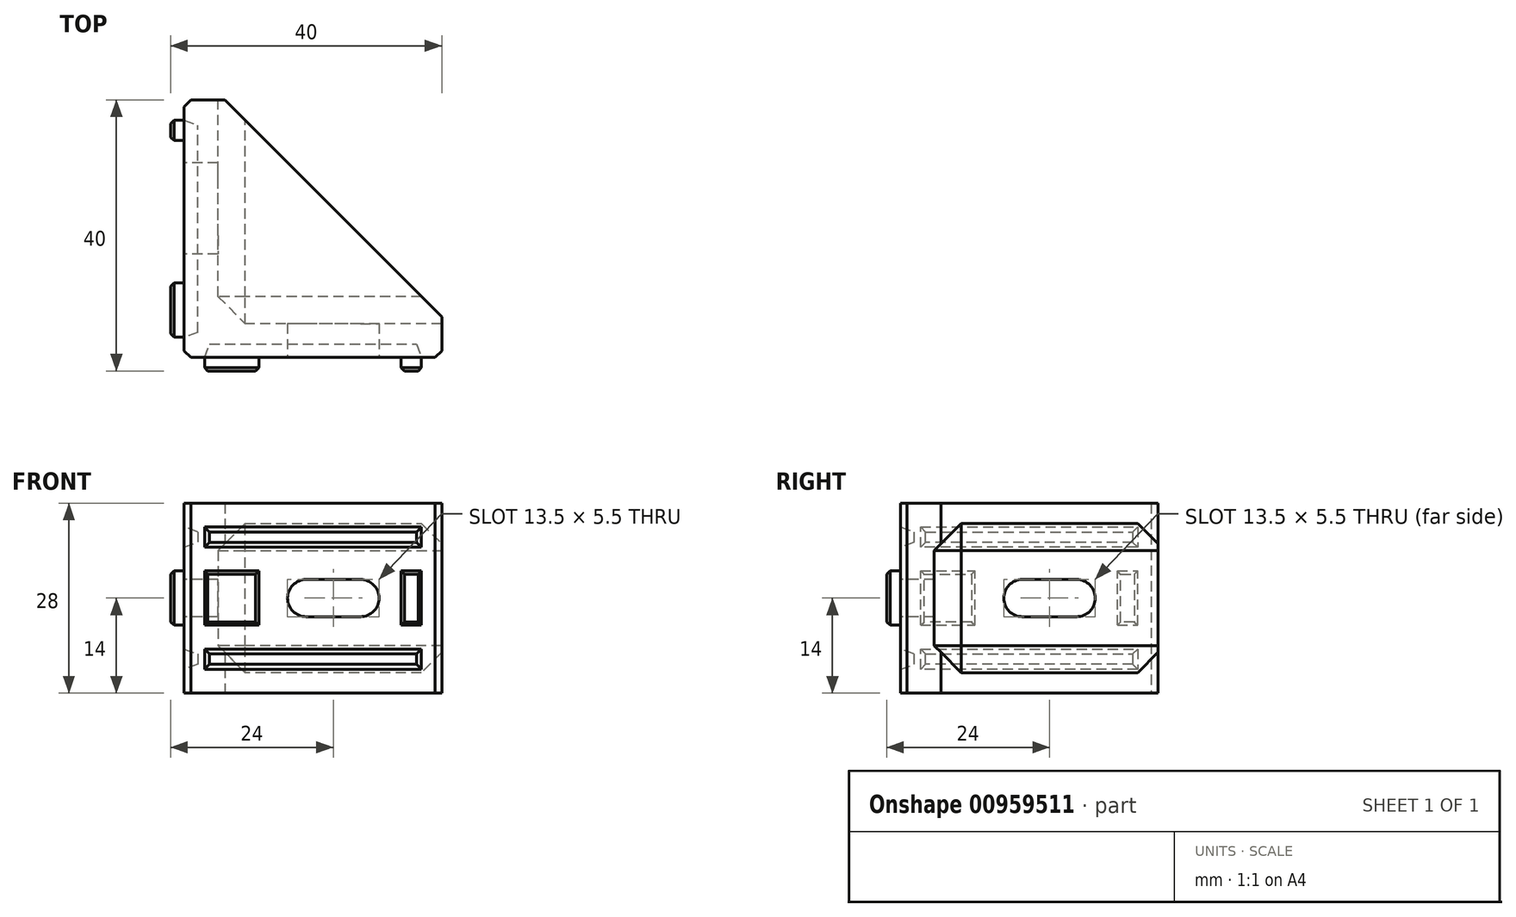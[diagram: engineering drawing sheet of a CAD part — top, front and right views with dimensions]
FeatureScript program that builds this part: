
annotation { "Feature Type Name" : "Feature", "Feature Type Description" : "" }
export const myFeature = defineFeature(function(context is Context, id is Id, definition is map)
    precondition{}
    {
        {
            var Q0;
            Q0=qCreatedBy(makeId("Top.planeOp"),FACE);
            var sketch = newSketch(context, id + "F0", { "sketchPlane" : qUnion([Q0])});
            skLineSegment(sketch, "E0.bottom", {"start": v(19, -19) * mm, "end": v(-19, -19) * mm});
            skLineSegment(sketch, "E0.top", {"start": v(-13, 19) * mm, "end": v(-19, 19) * mm});
            skLineSegment(sketch, "E0.left", {"start": v(19, -19) * mm, "end": v(19, -13) * mm});
            skLineSegment(sketch, "E0.right", {"start": v(-19, -19) * mm, "end": v(-19, 19) * mm});
            skPoint(sketch, "E0.middle", {"position": v(0, 0) * mm});
            skLineSegment(sketch, "E1", {"start": v(-13, 19) * mm, "end": v(19, -13) * mm});
            skSolve(sketch);
        }
        {
            var Q0;
            Q0 = qSketchRegion(id + "F0", true);
            extrude(context, id + "F1", {"entities" : qUnion([Q0]), "depth" : 28 * mm, "offsetDistance" : 25 * mm});
        }
        {
            var Q0;
            Q0=makeQuery(id+"F1.opExtrude","SWEPT_FACE",FACE,{"disambiguationData":[OSD([sQuery(id+"F0.wireOp",EDGE,"E0.left")])]});
            var sketch = newSketch(context, id + "F2", { "sketchPlane" : qUnion([Q0])});
            skLineSegment(sketch, "E2.0", {"start": v(19, 28) * mm, "end": v(19, 0) * mm});
            skLineSegment(sketch, "E3", {"start": v(19, 25) * mm, "end": v(-14, 25) * mm});
            skLineSegment(sketch, "E4", {"start": v(-14, 25) * mm, "end": v(-14, 3) * mm});
            skLineSegment(sketch, "E5", {"start": v(-14, 3) * mm, "end": v(19, 3) * mm});
            skSolve(sketch);
        }
        {
            var Q0;
            Q0 = qSketchRegion(id + "F2", true);
            var Q1;
            Q1=makeQuery(id+"F1.opExtrude","SWEPT_FACE",FACE,{"disambiguationData":[OSD([sQuery(id+"F0.wireOp",EDGE,"E0.right")])]});
            extrude(context, id + "F3", {"entities" : qUnion([Q0]), "operationType" : NewBodyOperationType.REMOVE, "endBound" : BoundingType.UP_TO_SURFACE, "oppositeDirection" : true, "depth" : 25 * mm, "endBoundEntityFace" : qUnion([Q1]), "hasOffset" : true, "offsetDistance" : 5 * mm});
        }
        {
            var Q0;
            Q0=makeQuery(id+"F1.opExtrude","SWEPT_FACE",FACE,{"disambiguationData":[OSD([sQuery(id+"F0.wireOp",EDGE,"E0.bottom")])]});
            var sketch = newSketch(context, id + "F4", { "sketchPlane" : qUnion([Q0])});
            skLineSegment(sketch, "E6.0", {"start": v(-14, 25) * mm, "end": v(-14, 3) * mm, "construction": true});
            skLineSegment(sketch, "E7", {"start": v(19, 14) * mm, "end": v(-14, 14) * mm, "construction": true});
            skArc(sketch, "E8", {"start": v(7, 11.25) * mm, "mid": v(9.75, 14) * mm, "end": v(7, 16.75) * mm});
            skArc(sketch, "E9", {"start": v(-1, 16.75) * mm, "mid": v(-3.75, 14) * mm, "end": v(-1, 11.25) * mm});
            skLineSegment(sketch, "E10", {"start": v(7, 16.75) * mm, "end": v(-1, 16.75) * mm});
            skLineSegment(sketch, "E11", {"start": v(7, 11.25) * mm, "end": v(-1, 11.25) * mm});
            skLineSegment(sketch, "E12.bottom", {"start": v(-8, 10) * mm, "end": v(-16, 10) * mm});
            skLineSegment(sketch, "E12.top", {"start": v(-8, 18) * mm, "end": v(-16, 18) * mm});
            skLineSegment(sketch, "E12.left", {"start": v(-8, 10) * mm, "end": v(-8, 18) * mm});
            skLineSegment(sketch, "E12.right", {"start": v(-16, 10) * mm, "end": v(-16, 18) * mm});
            skPoint(sketch, "E12.middle", {"position": v(-12, 14) * mm});
            skLineSegment(sketch, "E13.bottom", {"start": v(16, 10) * mm, "end": v(13, 10) * mm});
            skLineSegment(sketch, "E13.top", {"start": v(16, 18) * mm, "end": v(13, 18) * mm});
            skLineSegment(sketch, "E13.left", {"start": v(16, 10) * mm, "end": v(16, 18) * mm});
            skLineSegment(sketch, "E13.right", {"start": v(13, 10) * mm, "end": v(13, 18) * mm});
            skPoint(sketch, "E13.middle", {"position": v(14.5, 14) * mm});
            skLineSegment(sketch, "E14.bottom", {"start": v(-16, 24.5) * mm, "end": v(16, 24.5) * mm});
            skLineSegment(sketch, "E14.top", {"start": v(-16, 21.5) * mm, "end": v(16, 21.5) * mm});
            skLineSegment(sketch, "E14.left", {"start": v(-16, 24.5) * mm, "end": v(-16, 21.5) * mm});
            skLineSegment(sketch, "E14.right", {"start": v(16, 24.5) * mm, "end": v(16, 21.5) * mm});
            skLineSegment(sketch, "E15.MirrorCS", {"start": v(-16, 6.5) * mm, "end": v(16, 6.5) * mm});
            skLineSegment(sketch, "E16.MirrorCS", {"start": v(-16, 3.5) * mm, "end": v(16, 3.5) * mm});
            skLineSegment(sketch, "E17.MirrorCS", {"start": v(-16, 3.5) * mm, "end": v(-16, 6.5) * mm});
            skLineSegment(sketch, "E18.MirrorCS", {"start": v(16, 3.5) * mm, "end": v(16, 6.5) * mm});
            skSolve(sketch);
        }
        {
            var Q0;
            Q0=makeQuery(id+"F1.opExtrude","SWEPT_FACE",FACE,{"disambiguationData":[OSD([sQuery(id+"F0.wireOp",EDGE,"E0.right")])]});
            var sketch = newSketch(context, id + "F5", { "sketchPlane" : qUnion([Q0])});
            skLineSegment(sketch, "E19", {"start": v(14, 14) * mm, "end": v(-19, 14) * mm, "construction": true});
            skArc(sketch, "E20", {"start": v(1, 11.25) * mm, "mid": v(3.75, 14) * mm, "end": v(1, 16.75) * mm});
            skArc(sketch, "E21", {"start": v(-7, 16.75) * mm, "mid": v(-9.75, 14) * mm, "end": v(-7, 11.25) * mm});
            skLineSegment(sketch, "E22", {"start": v(1, 16.75) * mm, "end": v(-7, 16.75) * mm});
            skLineSegment(sketch, "E23", {"start": v(1, 11.25) * mm, "end": v(-7, 11.25) * mm});
            skLineSegment(sketch, "E24.0", {"start": v(14, 25) * mm, "end": v(14, 3) * mm, "construction": true});
            skLineSegment(sketch, "E25.bottom", {"start": v(16, 10) * mm, "end": v(8, 10) * mm});
            skLineSegment(sketch, "E25.top", {"start": v(16, 18) * mm, "end": v(8, 18) * mm});
            skLineSegment(sketch, "E25.left", {"start": v(16, 10) * mm, "end": v(16, 18) * mm});
            skLineSegment(sketch, "E25.right", {"start": v(8, 10) * mm, "end": v(8, 18) * mm});
            skPoint(sketch, "E25.middle", {"position": v(12, 14) * mm});
            skLineSegment(sketch, "E26.bottom", {"start": v(-13, 10) * mm, "end": v(-16, 10) * mm});
            skLineSegment(sketch, "E26.top", {"start": v(-13, 18) * mm, "end": v(-16, 18) * mm});
            skLineSegment(sketch, "E26.left", {"start": v(-13, 10) * mm, "end": v(-13, 18) * mm});
            skLineSegment(sketch, "E26.right", {"start": v(-16, 10) * mm, "end": v(-16, 18) * mm});
            skPoint(sketch, "E26.middle", {"position": v(-14.5, 14) * mm});
            skLineSegment(sketch, "E27.bottom", {"start": v(-16, 21.5) * mm, "end": v(16, 21.5) * mm});
            skLineSegment(sketch, "E27.top", {"start": v(-16, 24.5) * mm, "end": v(16, 24.5) * mm});
            skLineSegment(sketch, "E27.left", {"start": v(-16, 21.5) * mm, "end": v(-16, 24.5) * mm});
            skLineSegment(sketch, "E27.right", {"start": v(16, 21.5) * mm, "end": v(16, 24.5) * mm});
            skLineSegment(sketch, "E28.MirrorCS", {"start": v(-16, 6.5) * mm, "end": v(16, 6.5) * mm});
            skLineSegment(sketch, "E29.MirrorCS", {"start": v(16, 6.5) * mm, "end": v(16, 3.5) * mm});
            skLineSegment(sketch, "E30.MirrorCS", {"start": v(-16, 3.5) * mm, "end": v(16, 3.5) * mm});
            skLineSegment(sketch, "E31.MirrorCS", {"start": v(-16, 6.5) * mm, "end": v(-16, 3.5) * mm});
            skSolve(sketch);
        }
        {
            var Q0;
            Q0=makeQuery(id+"F4.imprint","IMPRINT",FACE,{"disambiguationData":[TD([[makeQuery(id+"F4.imprint","IMPRINT",EDGE,{"derivedFrom":sQuery(id+"F4.wireOp",EDGE,"E8")}),1.0]])]});
            var Q1;
            Q1 = qConstructionFilter(qBodyType(qCreatedBy(id + "F4" ,EDGE), BodyType.WIRE), ConstructionObject.NO);
            extrude(context, id + "F6", {"entities" : qUnion([Q0]), "operationType" : NewBodyOperationType.REMOVE, "surfaceEntities" : qUnion([Q1]), "oppositeDirection" : true, "depth" : 25 * mm, "offsetDistance" : 25 * mm});
        }
        {
            var Q0;
            Q0=makeQuery(id+"F5.imprint","IMPRINT",FACE,{"disambiguationData":[TD([[makeQuery(id+"F5.imprint","IMPRINT",EDGE,{"derivedFrom":sQuery(id+"F5.wireOp",EDGE,"E20")}),1.0]])]});
            extrude(context, id + "F7", {"entities" : qUnion([Q0]), "operationType" : NewBodyOperationType.REMOVE, "oppositeDirection" : true, "depth" : 25 * mm, "offsetDistance" : 25 * mm});
        }
        {
            var Q0;
            Q0=makeQuery(id+"F4.imprint","IMPRINT",FACE,{"disambiguationData":[TD([[makeQuery(id+"F4.imprint","IMPRINT",EDGE,{"derivedFrom":sQuery(id+"F4.wireOp",EDGE,"E12.bottom")}),-1.0]])]});
            var Q1;
            Q1=makeQuery(id+"F4.imprint","IMPRINT",FACE,{"disambiguationData":[TD([[makeQuery(id+"F4.imprint","IMPRINT",EDGE,{"derivedFrom":sQuery(id+"F4.wireOp",EDGE,"E13.bottom")}),-1.0]])]});
            extrude(context, id + "F8", {"entities" : qUnion([Q0, Q1]), "operationType" : NewBodyOperationType.ADD, "depth" : 2 * mm, "offsetDistance" : 25 * mm});
        }
        {
            var Q0;
            Q0=makeQuery(id+"F5.imprint","IMPRINT",FACE,{"disambiguationData":[TD([[makeQuery(id+"F5.imprint","IMPRINT",EDGE,{"derivedFrom":sQuery(id+"F5.wireOp",EDGE,"E27.bottom")}),1.0]])]});
            var Q1;
            Q1=makeQuery(id+"F5.imprint","IMPRINT",FACE,{"disambiguationData":[TD([[makeQuery(id+"F5.imprint","IMPRINT",EDGE,{"derivedFrom":sQuery(id+"F5.wireOp",EDGE,"E28.MirrorCS")}),-1.0]])]});
            extrude(context, id + "F9", {"entities" : qUnion([Q0, Q1]), "operationType" : NewBodyOperationType.REMOVE, "oppositeDirection" : true, "depth" : 2 * mm, "offsetDistance" : 25 * mm, "hasDraft" : true, "draftAngle" : 20 * degree, "draftPullDirection" : true});
        }
        {
            var Q0;
            Q0=makeQuery(id+"F5.imprint","IMPRINT",FACE,{"disambiguationData":[TD([[makeQuery(id+"F5.imprint","IMPRINT",EDGE,{"derivedFrom":sQuery(id+"F5.wireOp",EDGE,"E26.bottom")}),-1.0]])]});
            var Q1;
            Q1=makeQuery(id+"F5.imprint","IMPRINT",FACE,{"disambiguationData":[TD([[makeQuery(id+"F5.imprint","IMPRINT",EDGE,{"derivedFrom":sQuery(id+"F5.wireOp",EDGE,"E25.bottom")}),-1.0]])]});
            extrude(context, id + "F10", {"entities" : qUnion([Q0, Q1]), "operationType" : NewBodyOperationType.ADD, "depth" : 2 * mm, "offsetDistance" : 25 * mm});
        }
        {
            var Q0;
            Q0=makeQuery(id+"F4.imprint","IMPRINT",FACE,{"disambiguationData":[TD([[makeQuery(id+"F4.imprint","IMPRINT",EDGE,{"derivedFrom":sQuery(id+"F4.wireOp",EDGE,"E14.bottom")}),-1.0]])]});
            var Q1;
            Q1=makeQuery(id+"F4.imprint","IMPRINT",FACE,{"disambiguationData":[TD([[makeQuery(id+"F4.imprint","IMPRINT",EDGE,{"derivedFrom":sQuery(id+"F4.wireOp",EDGE,"E15.MirrorCS")}),-1.0]])]});
            extrude(context, id + "F11", {"entities" : qUnion([Q0, Q1]), "operationType" : NewBodyOperationType.REMOVE, "oppositeDirection" : true, "depth" : 2 * mm, "offsetDistance" : 25 * mm, "hasDraft" : true, "draftAngle" : 20 * degree, "draftPullDirection" : true});
        }
        {
            var Q0;
            Q0=makeQuery(id+"F1.opExtrude","SWEPT_EDGE",EDGE,{"disambiguationData":[OSD([sQuery(id+"F0.wireOp",EDGE,"E0.bottom"),sQuery(id+"F0.wireOp",EDGE,"E0.right")])]});
            var Q1;
            Q1=makeQuery(id+"F1.opExtrude","SWEPT_EDGE",EDGE,{"disambiguationData":[OSD([sQuery(id+"F0.wireOp",EDGE,"E0.bottom"),sQuery(id+"F0.wireOp",EDGE,"E0.left")])]});
            var Q2;
            Q2=makeQuery(id+"F1.opExtrude","SWEPT_EDGE",EDGE,{"disambiguationData":[OSD([sQuery(id+"F0.wireOp",EDGE,"E0.top"),sQuery(id+"F0.wireOp",EDGE,"E0.right")])]});
            chamfer(context, id + "F12", {"entities" : qUnion([Q0, Q1, Q2]), "width" : 1 * mm, "tangentPropagation" : true});
        }
        {
            var Q0;
            Q0=makeQuery(id+"F10.opExtrude","CAP_FACE",FACE,{"disambiguationData":[OSD([sQuery(id+"F5.wireOp",EDGE,"E26.bottom"),sQuery(id+"F5.wireOp",EDGE,"E26.top"),sQuery(id+"F5.wireOp",EDGE,"E26.left"),sQuery(id+"F5.wireOp",EDGE,"E26.right")])],"isStart":false});
            var Q1;
            Q1=makeQuery(id+"F10.opExtrude","CAP_FACE",FACE,{"disambiguationData":[OSD([sQuery(id+"F5.wireOp",EDGE,"E25.bottom"),sQuery(id+"F5.wireOp",EDGE,"E25.top"),sQuery(id+"F5.wireOp",EDGE,"E25.left"),sQuery(id+"F5.wireOp",EDGE,"E25.right")])],"isStart":false});
            var Q2;
            Q2=makeQuery(id+"F8.opExtrude","CAP_FACE",FACE,{"disambiguationData":[OSD([sQuery(id+"F4.wireOp",EDGE,"E12.bottom"),sQuery(id+"F4.wireOp",EDGE,"E12.top"),sQuery(id+"F4.wireOp",EDGE,"E12.left"),sQuery(id+"F4.wireOp",EDGE,"E12.right")])],"isStart":false});
            var Q3;
            Q3=makeQuery(id+"F8.opExtrude","CAP_FACE",FACE,{"disambiguationData":[OSD([sQuery(id+"F4.wireOp",EDGE,"E13.bottom"),sQuery(id+"F4.wireOp",EDGE,"E13.top"),sQuery(id+"F4.wireOp",EDGE,"E13.left"),sQuery(id+"F4.wireOp",EDGE,"E13.right")])],"isStart":false});
            var Q4;
            Q4=makeQuery(id+"F10.opExtrude","CAP_EDGE",EDGE,{"disambiguationData":[OSD([sQuery(id+"F5.wireOp",EDGE,"E26.left")])],"isStart":true});
            var Q5;
            Q5=makeQuery(id+"F10.opExtrude","CAP_EDGE",EDGE,{"disambiguationData":[OSD([sQuery(id+"F5.wireOp",EDGE,"E25.left")])],"isStart":true});
            var Q6;
            Q6=makeQuery(id+"F8.opExtrude","CAP_EDGE",EDGE,{"disambiguationData":[OSD([sQuery(id+"F4.wireOp",EDGE,"E12.right")])],"isStart":true});
            var Q7;
            Q7=makeQuery(id+"F8.opExtrude","CAP_EDGE",EDGE,{"disambiguationData":[OSD([sQuery(id+"F4.wireOp",EDGE,"E13.right")])],"isStart":true});
            var Q8;
            Q8=makeQuery(id+"F10.opExtrude","CAP_EDGE",EDGE,{"disambiguationData":[OSD([sQuery(id+"F5.wireOp",EDGE,"E25.right")])],"isStart":true});
            var Q9;
            Q9=makeQuery(id+"F10.opExtrude","CAP_EDGE",EDGE,{"disambiguationData":[OSD([sQuery(id+"F5.wireOp",EDGE,"E26.right")])],"isStart":true});
            var Q10;
            Q10=makeQuery(id+"F8.opExtrude","CAP_EDGE",EDGE,{"disambiguationData":[OSD([sQuery(id+"F4.wireOp",EDGE,"E13.left")])],"isStart":true});
            var Q11;
            Q11=makeQuery(id+"F8.opExtrude","CAP_EDGE",EDGE,{"disambiguationData":[OSD([sQuery(id+"F4.wireOp",EDGE,"E12.left")])],"isStart":true});
            chamfer(context, id + "F13", {"entities" : qUnion([Q0, Q1, Q2, Q3, Q4, Q5, Q6, Q7, Q8, Q9, Q10, Q11]), "width" : 0.5 * mm, "tangentPropagation" : true});
        }
        {
            var Q0;
            Q0=makeQuery(id+"F3.boolean.opBoolean","COPY",EDGE,{"derivedFrom":makeQuery(id+"F3.opExtrude","CAP_EDGE",EDGE,{"disambiguationData":[OSD([sQuery(id+"F2.wireOp",EDGE,"E5")])],"isStart":false})});
            var Q1;
            Q1=makeQuery(id+"F3.boolean.opBoolean","COPY",EDGE,{"derivedFrom":makeQuery(id+"F3.opExtrude","SWEPT_EDGE",EDGE,{"disambiguationData":[OSD([sQuery(id+"F2.wireOp",EDGE,"E4"),sQuery(id+"F2.wireOp",EDGE,"E5")])]})});
            var Q2;
            Q2=makeQuery(id+"F3.boolean.opBoolean","COPY",EDGE,{"derivedFrom":makeQuery(id+"F3.opExtrude","CAP_EDGE",EDGE,{"disambiguationData":[OSD([sQuery(id+"F2.wireOp",EDGE,"E3")])],"isStart":false})});
            var Q3;
            Q3=makeQuery(id+"F3.boolean.opBoolean","COPY",EDGE,{"derivedFrom":makeQuery(id+"F3.opExtrude","SWEPT_EDGE",EDGE,{"disambiguationData":[OSD([sQuery(id+"F2.wireOp",EDGE,"E3"),sQuery(id+"F2.wireOp",EDGE,"E4")])]})});
            var Q4;
            Q4=makeQuery(id+"F3.boolean.opBoolean","COPY",EDGE,{"derivedFrom":makeQuery(id+"F3.opExtrude","CAP_EDGE",EDGE,{"disambiguationData":[OSD([sQuery(id+"F2.wireOp",EDGE,"E4")])],"isStart":false})});
            chamfer(context, id + "F14", {"entities" : qUnion([Q0, Q1, Q2, Q3, Q4]), "width" : 4 * mm, "tangentPropagation" : true});
        }
    });
